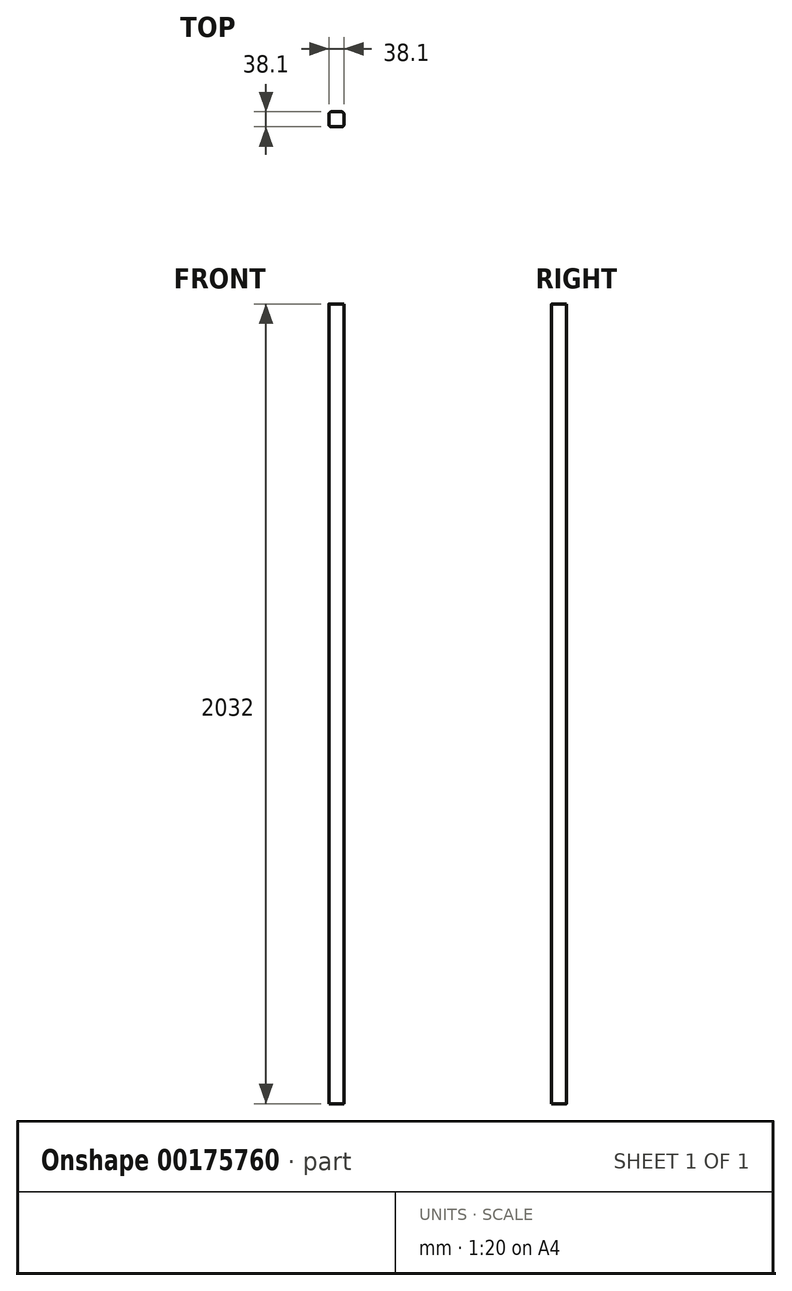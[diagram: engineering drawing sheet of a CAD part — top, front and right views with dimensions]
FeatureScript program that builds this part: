
annotation { "Feature Type Name" : "Feature", "Feature Type Description" : "" }
export const myFeature = defineFeature(function(context is Context, id is Id, definition is map)
    precondition{}
    {
        {
            var Q0;
            Q0=qCreatedBy(makeId("Top.planeOp"),FACE);
            var sketch = newSketch(context, id + "F0", { "sketchPlane" : qUnion([Q0])});
            skLineSegment(sketch, "E0.bottom", {"start": v(12.7, 19.05) * mm, "end": v(-12.7, 19.05) * mm});
            skLineSegment(sketch, "E0.top", {"start": v(12.7, -19.05) * mm, "end": v(-12.7, -19.05) * mm});
            skLineSegment(sketch, "E0.left", {"start": v(19.05, 12.7) * mm, "end": v(19.05, -12.7) * mm});
            skLineSegment(sketch, "E0.right", {"start": v(-19.05, 12.7) * mm, "end": v(-19.05, -12.7) * mm});
            skPoint(sketch, "E0.middle", {"position": v(0, 0) * mm});
            skPoint(sketch, "E1.visualSharp", {"position": v(-19.05, 19.05) * mm});
            skArc(sketch, "E1.filletArc", {"start": v(-12.7, 19.05) * mm, "mid": v(-17.2, 17.2) * mm, "end": v(-19.05, 12.7) * mm});
            skPoint(sketch, "E2.visualSharp", {"position": v(19.05, 19.05) * mm});
            skArc(sketch, "E2.filletArc", {"start": v(19.05, 12.7) * mm, "mid": v(17.2, 17.2) * mm, "end": v(12.7, 19.05) * mm});
            skPoint(sketch, "E3.visualSharp", {"position": v(19.05, -19.05) * mm});
            skArc(sketch, "E3.filletArc", {"start": v(12.7, -19.05) * mm, "mid": v(17.2, -17.2) * mm, "end": v(19.05, -12.7) * mm});
            skPoint(sketch, "E4.visualSharp", {"position": v(-19.05, -19.05) * mm});
            skArc(sketch, "E4.filletArc", {"start": v(-19.05, -12.7) * mm, "mid": v(-17.2, -17.2) * mm, "end": v(-12.7, -19.05) * mm});
            skSolve(sketch);
        }
        {
            var Q0;
            Q0=qSketchRegion(id+"F0",true);
            extrude(context, id + "F1", {"entities" : qUnion([Q0]), "depth" : 2032 * mm, "offsetDistance" : 25.4 * mm});
        }
    });
